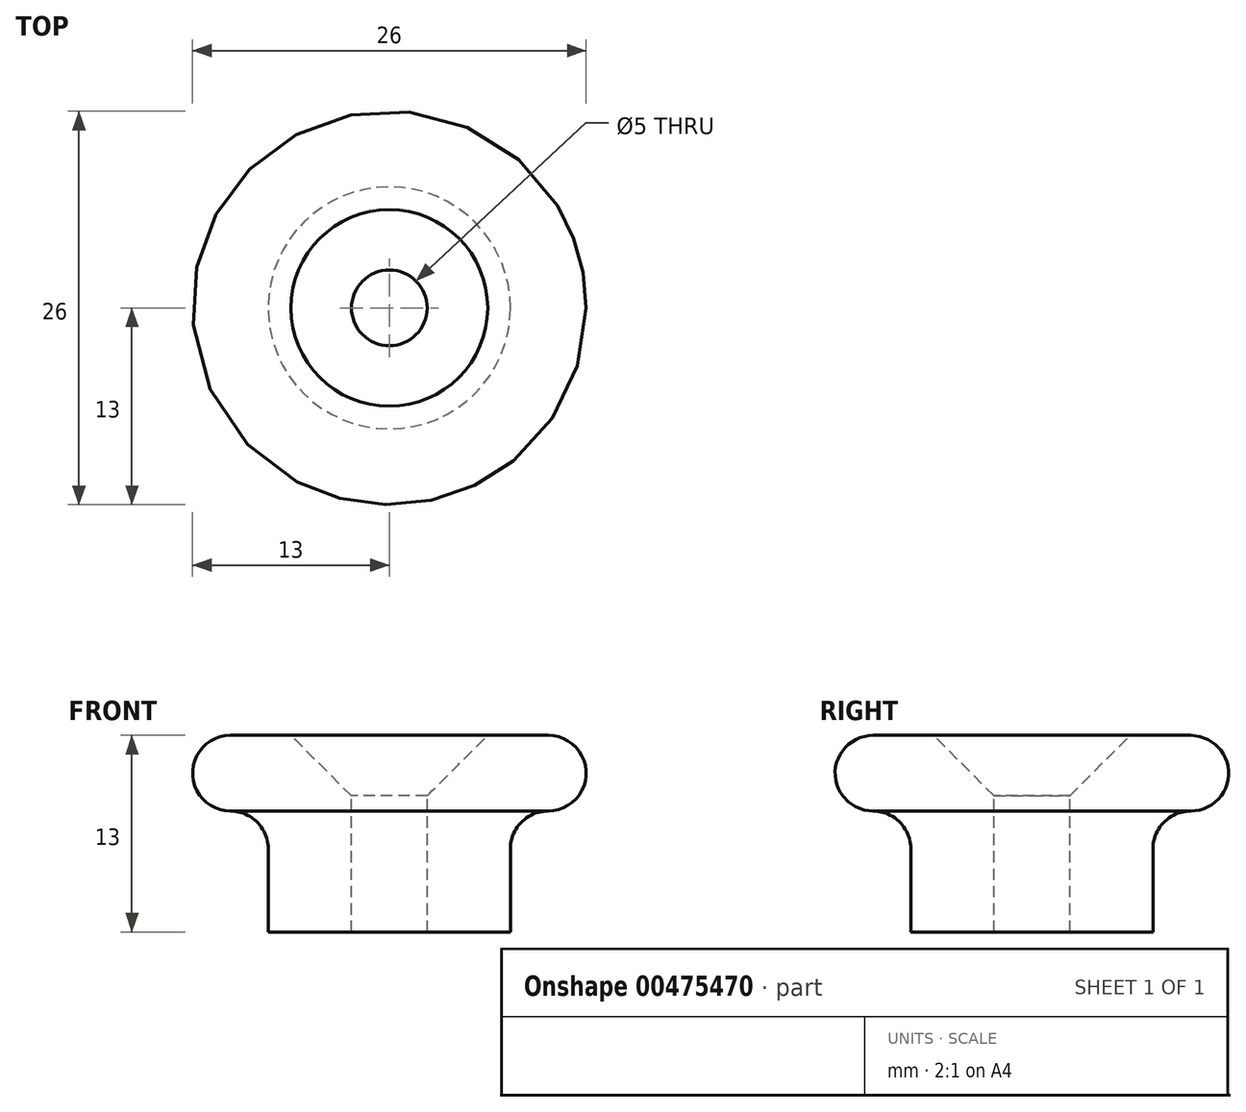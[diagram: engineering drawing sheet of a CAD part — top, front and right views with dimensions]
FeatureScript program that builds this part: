
annotation { "Feature Type Name" : "Feature", "Feature Type Description" : "" }
export const myFeature = defineFeature(function(context is Context, id is Id, definition is map)
    precondition{}
    {
        {
            var Q0;
            Q0=qCreatedBy(makeId("Front.planeOp"),FACE);
            var sketch = newSketch(context, id + "F0", { "sketchPlane" : qUnion([Q0])});
            skLineSegment(sketch, "E0", {"start": v(0, 0) * mm, "end": v(-8, 0) * mm});
            skLineSegment(sketch, "E1", {"start": v(-8, 0) * mm, "end": v(-8, 5.5) * mm});
            skLineSegment(sketch, "E2", {"start": v(-10.5, 8) * mm, "end": v(-10.5, 8) * mm});
            skLineSegment(sketch, "E3", {"start": v(-13, 10.5) * mm, "end": v(-13, 10.5) * mm});
            skLineSegment(sketch, "E4", {"start": v(-10.5, 13) * mm, "end": v(0, 13) * mm});
            skLineSegment(sketch, "E5", {"start": v(0, 13) * mm, "end": v(0, 0) * mm});
            skPoint(sketch, "E6.visualSharp", {"position": v(-13, 13) * mm});
            skArc(sketch, "E6.filletArc", {"start": v(-10.5, 13) * mm, "mid": v(-12.27, 12.27) * mm, "end": v(-13, 10.5) * mm});
            skPoint(sketch, "E7.visualSharp", {"position": v(-13, 8) * mm});
            skArc(sketch, "E7.filletArc", {"start": v(-13, 10.5) * mm, "mid": v(-12.27, 8.73) * mm, "end": v(-10.5, 8) * mm});
            skPoint(sketch, "E8.visualSharp", {"position": v(-8, 8) * mm});
            skArc(sketch, "E8.filletArc", {"start": v(-8, 5.5) * mm, "mid": v(-8.73, 7.27) * mm, "end": v(-10.5, 8) * mm});
            skSolve(sketch);
        }
        {
            var Q0;
            Q0=makeQuery(id+"F0.imprint","IMPRINT",FACE,{"disambiguationData":[TD([[makeQuery(id+"F0.imprint","IMPRINT",EDGE,{"derivedFrom":sQuery(id+"F0.wireOp",EDGE,"E0")}),-1.0]])]});
            var Q1;
            Q1=sQuery(id+"F0.wireOp",EDGE,"E5");
            revolve(context, id + "F1", {"entities" : qUnion([Q0]), "axis" : qUnion([Q1]), "revolveType" : RevolveType.FULL});
        }
        {
            var Q0;
            Q0=makeQuery(id+"F1.opRevolve","SWEPT_FACE",FACE,{"disambiguationData":[OSD([sQuery(id+"F0.wireOp",EDGE,"E4")])]});
            var sketch = newSketch(context, id + "F2", { "sketchPlane" : qUnion([Q0])});
            skPoint(sketch, "E9", {"position": v(0, 0) * mm});
            skSolve(sketch);
        }
        {
            var Q0;
            Q0=sQuery(id+"F2.wireOp",VERTEX,"E9");
            var Q1;
            Q1=makeQuery(id+"F1.opRevolve","SWEPT_BODY",BODY,{"disambiguationData":[OSD([sQuery(id+"F0.wireOp",EDGE,"E0"),sQuery(id+"F0.wireOp",EDGE,"E1"),sQuery(id+"F0.wireOp",EDGE,"E4"),sQuery(id+"F0.wireOp",EDGE,"E5"),sQuery(id+"F0.wireOp",EDGE,"E6.filletArc"),sQuery(id+"F0.wireOp",EDGE,"E7.filletArc"),sQuery(id+"F0.wireOp",EDGE,"E8.filletArc")])]});
            hole(context, id + "F3", {"style" : HoleStyle.C_SINK, "endStyle" : HoleEndStyle.THROUGH, "holeDiameter" : 5 * mm, "cSinkDiameter" : 13 * mm, "cSinkAngle" : 90 * degree, "majorDiameter" : 5 * mm, "isTappedThrough" : true, "tappedDepth" : 12 * mm, "tapClearance" : 3, "locations" : qUnion([Q0]), "scope" : qUnion([Q1])});
        }
    });
